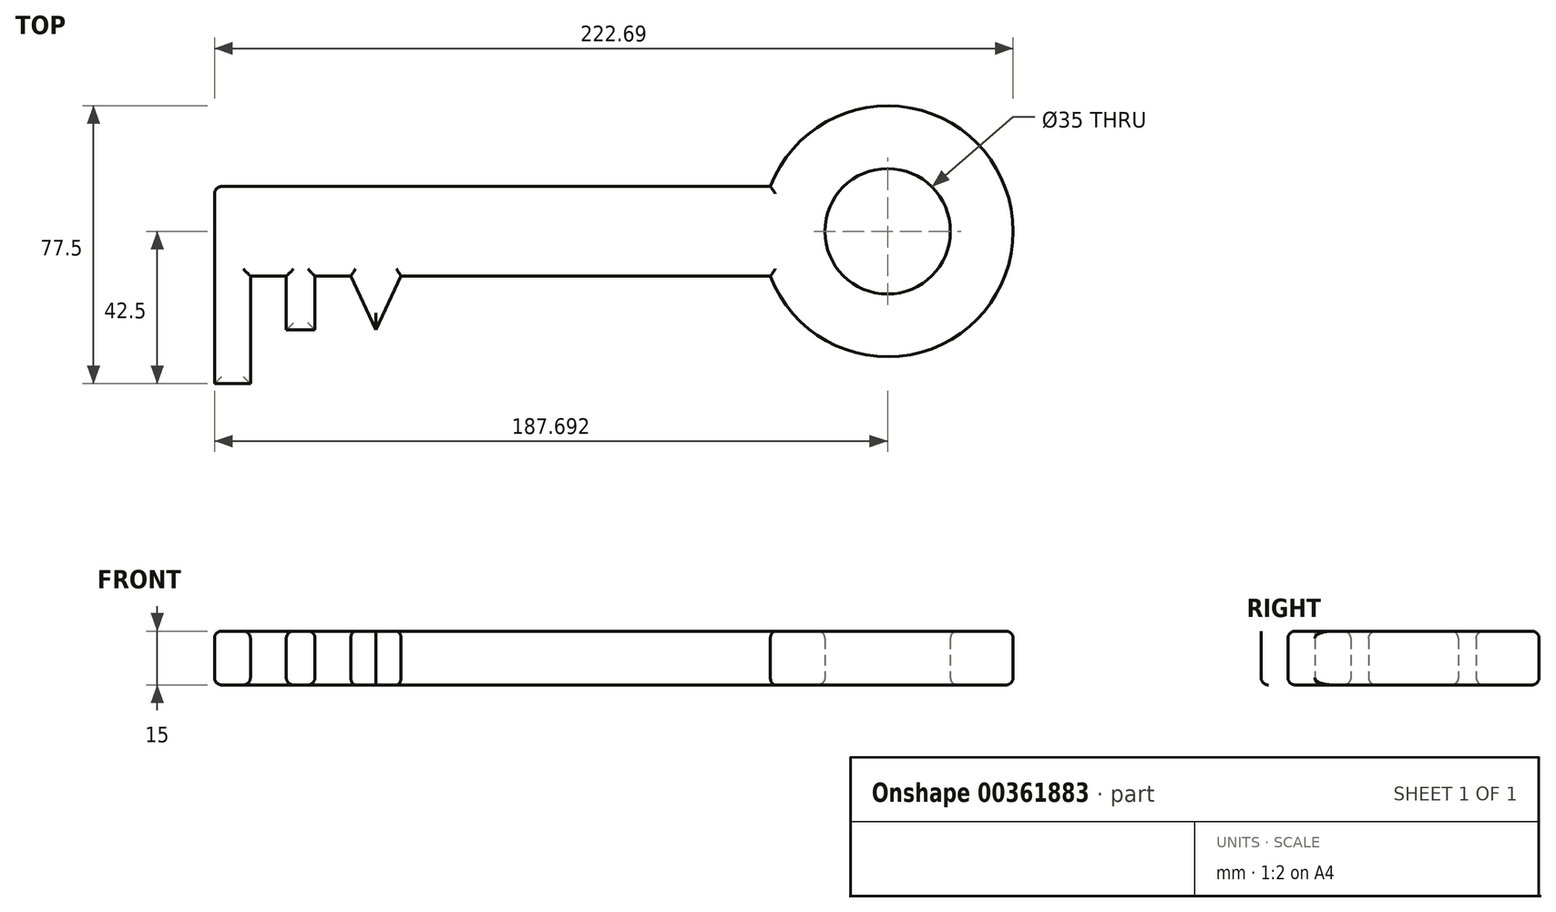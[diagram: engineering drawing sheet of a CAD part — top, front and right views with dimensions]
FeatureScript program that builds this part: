
annotation { "Feature Type Name" : "Feature", "Feature Type Description" : "" }
export const myFeature = defineFeature(function(context is Context, id is Id, definition is map)
    precondition{}
    {
        {
            var Q0;
            Q0=qCreatedBy(makeId("Top.planeOp"),FACE);
            var sketch = newSketch(context, id + "F0", { "sketchPlane" : qUnion([Q0])});
            skLineSegment(sketch, "E0.bottom", {"start": v(0, 25) * mm, "end": v(-155, 25) * mm});
            skLineSegment(sketch, "E0.top", {"start": v(0, 0) * mm, "end": v(-155, 0) * mm});
            skLineSegment(sketch, "E0.left", {"start": v(0, 25) * mm, "end": v(0, 0) * mm});
            skLineSegment(sketch, "E0.right", {"start": v(-155, 25) * mm, "end": v(-155, 0) * mm});
            skLineSegment(sketch, "E1.bottom", {"start": v(-155, 0) * mm, "end": v(-145, 0) * mm});
            skLineSegment(sketch, "E1.top", {"start": v(-155, -30) * mm, "end": v(-145, -30) * mm});
            skLineSegment(sketch, "E1.left", {"start": v(-155, 0) * mm, "end": v(-155, -30) * mm});
            skLineSegment(sketch, "E1.right", {"start": v(-145, 0) * mm, "end": v(-145, -30) * mm});
            skLineSegment(sketch, "E2.bottom", {"start": v(-135, 0) * mm, "end": v(-127, 0) * mm});
            skLineSegment(sketch, "E2.top", {"start": v(-135, -15) * mm, "end": v(-127, -15) * mm});
            skLineSegment(sketch, "E2.left", {"start": v(-135, 0) * mm, "end": v(-135, -15) * mm});
            skLineSegment(sketch, "E2.right", {"start": v(-127, 0) * mm, "end": v(-127, -15) * mm});
            skLineSegment(sketch, "E3", {"start": v(-117, 0) * mm, "end": v(-110, -15) * mm});
            skLineSegment(sketch, "E4", {"start": v(-110, -15) * mm, "end": v(-103, 0) * mm});
            skArc(sketch, "E5", {"start": v(0, 0) * mm, "mid": v(67.7, 12.5) * mm, "end": v(0, 25) * mm});
            skCircle(sketch, "E6", {"center": v(32.7, 12.5) * mm, "radius": 17.5 * mm});
            skLineSegment(sketch, "E7", {"start": v(-155, 12.5) * mm, "end": v(32.7, 12.5) * mm, "construction": true});
            skSolve(sketch);
        }
        {
            var Q0;
            Q0=makeQuery(id+"F0.imprint","IMPRINT",FACE,{"disambiguationData":[TD([[makeQuery(id+"F0.imprint","IMPRINT",EDGE,{"derivedFrom":sQuery(id+"F0.wireOp",EDGE,"E0.bottom")}),1.0]])]});
            var Q1;
            Q1=makeQuery(id+"F0.imprint","IMPRINT",FACE,{"disambiguationData":[TD([[makeQuery(id+"F0.imprint","IMPRINT",EDGE,{"derivedFrom":sQuery(id+"F0.wireOp",EDGE,"E0.left")}),1.0]])]});
            var Q2;
            Q2=makeQuery(id+"F0.imprint","IMPRINT",FACE,{"disambiguationData":[TD([[makeQuery(id+"F0.imprint","IMPRINT",EDGE,{"derivedFrom":sQuery(id+"F0.wireOp",EDGE,"E1.bottom")}),-1.0]])]});
            var Q3;
            Q3=makeQuery(id+"F0.imprint","IMPRINT",FACE,{"disambiguationData":[TD([[makeQuery(id+"F0.imprint","IMPRINT",EDGE,{"derivedFrom":sQuery(id+"F0.wireOp",EDGE,"E2.bottom")}),-1.0]])]});
            var Q4;
            {var subQ0=sQuery(id+"F0.wireOp",EDGE,"E3");Q4=makeQuery(id+"F0.imprint","IMPRINT",FACE,{"disambiguationData":[TD([[makeQuery(id+"F0.imprint","IMPRINT",EDGE,{"derivedFrom":subQ0}),1.0]])]});}
            extrude(context, id + "F1", {"entities" : qUnion([Q0, Q1, Q2, Q3, Q4]), "depth" : 15 * mm});
        }
        {
            var Q0;
            Q0=makeQuery(id+"F1.opExtrude","CAP_EDGE",EDGE,{"disambiguationData":[OSD([sQuery(id+"F0.wireOp",EDGE,"E0.bottom")])],"isStart":false});
            var Q1;
            Q1=makeQuery(id+"F1.opExtrude","CAP_EDGE",EDGE,{"disambiguationData":[OSD([sQuery(id+"F0.wireOp",EDGE,"E0.bottom")])],"isStart":true});
            var Q2;
            Q2=makeQuery(id+"F1.opExtrude","CAP_EDGE",EDGE,{"disambiguationData":[OSD([sQuery(id+"F0.wireOp",EDGE,"E0.right"),sQuery(id+"F0.wireOp",EDGE,"E1.left")])],"isStart":true});
            var Q3;
            Q3=makeQuery(id+"F1.opExtrude","CAP_EDGE",EDGE,{"disambiguationData":[OSD([sQuery(id+"F0.wireOp",EDGE,"E0.right"),sQuery(id+"F0.wireOp",EDGE,"E1.left")])],"isStart":false});
            var Q4;
            {var subQ0=sQuery(id+"F0.wireOp",EDGE,"E0.top");Q4=makeQuery(id+"F1.opExtrude","CAP_EDGE",EDGE,{"disambiguationData":[OSD([subQ0]),TDD([makeQuery(id+"F0.imprint","IMPRINT",EDGE,{"disambiguationData":[TD([[makeQuery(id+"F0.imprint","INTERSECT",VERTEX,{"derivedFrom":[subQ0,sQuery(id+"F0.wireOp",EDGE,"E4")]}),1.0]])],"derivedFrom":subQ0})])],"isStart":true});}
            var Q5;
            Q5=makeQuery(id+"F1.opExtrude","CAP_FACE",FACE,{"disambiguationData":[OSD([sQuery(id+"F0.wireOp",EDGE,"E0.bottom"),sQuery(id+"F0.wireOp",EDGE,"E0.top"),sQuery(id+"F0.wireOp",EDGE,"E0.right"),sQuery(id+"F0.wireOp",EDGE,"E1.top"),sQuery(id+"F0.wireOp",EDGE,"E1.left"),sQuery(id+"F0.wireOp",EDGE,"E1.right"),sQuery(id+"F0.wireOp",EDGE,"E2.top"),sQuery(id+"F0.wireOp",EDGE,"E2.left"),sQuery(id+"F0.wireOp",EDGE,"E2.right"),sQuery(id+"F0.wireOp",EDGE,"E3"),sQuery(id+"F0.wireOp",EDGE,"E4"),sQuery(id+"F0.wireOp",EDGE,"E5"),sQuery(id+"F0.wireOp",EDGE,"E6")])],"isStart":false});
            fillet(context, id + "F2", {"entities" : qUnion([Q0, Q1, Q2, Q3, Q4, Q5]), "radius" : 2 * mm, "tangentPropagation" : true, "allowEdgeOverflow" : false});
        }
        {
            var Q0;
            Q0 = qSketchRegion(id + "F0", true);
            extrude(context, id + "F3", {"entities" : qUnion([Q0]), "operationType" : NewBodyOperationType.ADD, "depth" : 15 * mm});
        }
        {
            var Q0;
            Q0=makeQuery(id+"F3.opExtrude","CAP_EDGE",EDGE,{"disambiguationData":[OSD([sQuery(id+"F0.wireOp",EDGE,"E0.bottom")])],"isStart":false});
            var Q1;
            Q1=makeQuery(id+"F3.opExtrude","CAP_EDGE",EDGE,{"disambiguationData":[OSD([sQuery(id+"F0.wireOp",EDGE,"E0.right"),sQuery(id+"F0.wireOp",EDGE,"E1.left")])],"isStart":false});
            var Q2;
            Q2=makeQuery(id+"F3.opExtrude","CAP_EDGE",EDGE,{"disambiguationData":[OSD([sQuery(id+"F0.wireOp",EDGE,"E1.right")])],"isStart":false});
            var Q3;
            Q3=makeQuery(id+"F3.opExtrude","CAP_EDGE",EDGE,{"disambiguationData":[OSD([sQuery(id+"F0.wireOp",EDGE,"E2.left")])],"isStart":false});
            var Q4;
            Q4=makeQuery(id+"F3.opExtrude","CAP_EDGE",EDGE,{"disambiguationData":[OSD([sQuery(id+"F0.wireOp",EDGE,"E2.right")])],"isStart":false});
            var Q5;
            Q5=makeQuery(id+"F3.opExtrude","CAP_EDGE",EDGE,{"disambiguationData":[OSD([sQuery(id+"F0.wireOp",EDGE,"E3")])],"isStart":false});
            var Q6;
            Q6=makeQuery(id+"F3.opExtrude","CAP_EDGE",EDGE,{"disambiguationData":[OSD([sQuery(id+"F0.wireOp",EDGE,"E4")])],"isStart":false});
            var Q7;
            {var subQ0=sQuery(id+"F0.wireOp",EDGE,"E0.top");Q7=makeQuery(id+"F3.opExtrude","CAP_EDGE",EDGE,{"disambiguationData":[OSD([subQ0]),TDD([makeQuery(id+"F0.imprint","IMPRINT",EDGE,{"disambiguationData":[TD([[makeQuery(id+"F0.imprint","INTERSECT",VERTEX,{"derivedFrom":[subQ0,sQuery(id+"F0.wireOp",EDGE,"E4")]}),1.0]])],"derivedFrom":subQ0})])],"isStart":false});}
            var Q8;
            {var subQ0=sQuery(id+"F0.wireOp",EDGE,"E0.top");Q8=makeQuery(id+"F3.opExtrude","CAP_EDGE",EDGE,{"disambiguationData":[OSD([subQ0]),TDD([makeQuery(id+"F0.imprint","IMPRINT",EDGE,{"disambiguationData":[TD([[makeQuery(id+"F0.imprint","INTERSECT",VERTEX,{"derivedFrom":[subQ0,sQuery(id+"F0.wireOp",EDGE,"E3")]}),-1.0]])],"derivedFrom":subQ0})])],"isStart":false});}
            var Q9;
            {var subQ0=sQuery(id+"F0.wireOp",EDGE,"E0.top");Q9=makeQuery(id+"F3.opExtrude","CAP_EDGE",EDGE,{"disambiguationData":[OSD([subQ0]),TDD([makeQuery(id+"F0.imprint","IMPRINT",EDGE,{"disambiguationData":[TD([[makeQuery(id+"F0.imprint","INTERSECT",VERTEX,{"derivedFrom":[subQ0,sQuery(id+"F0.wireOp",EDGE,"E1.bottom"),sQuery(id+"F0.wireOp",EDGE,"E1.right")]}),1.0]])],"derivedFrom":subQ0})])],"isStart":false});}
            var Q10;
            {var subQ0=sQuery(id+"F0.wireOp",EDGE,"E1.left");var subQ1=sQuery(id+"F0.wireOp",EDGE,"E1.top");Q10=makeQuery(id+"F3.boolean.opBoolean","MERGE",EDGE,{"derivedFrom":[makeQuery(id+"F1.opExtrude","SWEPT_EDGE",EDGE,{"disambiguationData":[OSD([subQ1,subQ0])]}),makeQuery(id+"F3.opExtrude","SWEPT_EDGE",EDGE,{"disambiguationData":[OSD([subQ1,subQ0])]})]});}
            var Q11;
            Q11=makeQuery(id+"F3.opExtrude","CAP_EDGE",EDGE,{"disambiguationData":[OSD([sQuery(id+"F0.wireOp",EDGE,"E0.right"),sQuery(id+"F0.wireOp",EDGE,"E1.left")])],"isStart":true});
            var Q12;
            {var subQ0=sQuery(id+"F0.wireOp",EDGE,"E0.right");var subQ1=sQuery(id+"F0.wireOp",EDGE,"E0.bottom");Q12=makeQuery(id+"F3.boolean.opBoolean","MERGE",EDGE,{"derivedFrom":[makeQuery(id+"F1.opExtrude","SWEPT_EDGE",EDGE,{"disambiguationData":[OSD([subQ1,subQ0])]}),makeQuery(id+"F3.opExtrude","SWEPT_EDGE",EDGE,{"disambiguationData":[OSD([subQ1,subQ0])]})]});}
            var Q13;
            Q13=makeQuery(id+"F3.opExtrude","CAP_EDGE",EDGE,{"disambiguationData":[OSD([sQuery(id+"F0.wireOp",EDGE,"E5")])],"isStart":false});
            var Q14;
            Q14=makeQuery(id+"F3.opExtrude","CAP_EDGE",EDGE,{"disambiguationData":[OSD([sQuery(id+"F0.wireOp",EDGE,"E6")])],"isStart":false});
            var Q15;
            Q15=makeQuery(id+"F1.opExtrude","CAP_EDGE",EDGE,{"disambiguationData":[OSD([sQuery(id+"F0.wireOp",EDGE,"E6")])],"isStart":true});
            var Q16;
            Q16=makeQuery(id+"F1.opExtrude","CAP_EDGE",EDGE,{"disambiguationData":[OSD([sQuery(id+"F0.wireOp",EDGE,"E5")])],"isStart":true});
            var Q17;
            Q17=makeQuery(id+"F3.opExtrude","CAP_EDGE",EDGE,{"disambiguationData":[OSD([sQuery(id+"F0.wireOp",EDGE,"E0.bottom")])],"isStart":true});
            var Q18;
            {var subQ0=sQuery(id+"F0.wireOp",EDGE,"E6");var subQ1=sQuery(id+"F0.wireOp",EDGE,"E5");var subQ2=sQuery(id+"F0.wireOp",EDGE,"E4");var subQ3=sQuery(id+"F0.wireOp",EDGE,"E3");var subQ4=sQuery(id+"F0.wireOp",EDGE,"E2.right");var subQ5=sQuery(id+"F0.wireOp",EDGE,"E2.left");var subQ6=sQuery(id+"F0.wireOp",EDGE,"E2.top");var subQ7=sQuery(id+"F0.wireOp",EDGE,"E1.right");var subQ8=sQuery(id+"F0.wireOp",EDGE,"E1.left");var subQ9=sQuery(id+"F0.wireOp",EDGE,"E1.top");var subQ10=sQuery(id+"F0.wireOp",EDGE,"E0.right");var subQ11=sQuery(id+"F0.wireOp",EDGE,"E0.top");var subQ12=sQuery(id+"F0.wireOp",EDGE,"E0.bottom");Q18=makeQuery(id+"F3.boolean.opBoolean","MERGE",FACE,{"derivedFrom":[makeQuery(id+"F1.opExtrude","CAP_FACE",FACE,{"disambiguationData":[OSD([subQ12,subQ11,subQ10,subQ9,subQ8,subQ7,subQ6,subQ5,subQ4,subQ3,subQ2,subQ1,subQ0])],"isStart":true}),makeQuery(id+"F3.opExtrude","CAP_FACE",FACE,{"disambiguationData":[OSD([subQ12,subQ11,subQ10,subQ9,subQ8,subQ7,subQ6,subQ5,subQ4,subQ3,subQ2,subQ1,subQ0])],"isStart":true})]});}
            fillet(context, id + "F4", {"entities" : qUnion([Q0, Q1, Q2, Q3, Q4, Q5, Q6, Q7, Q8, Q9, Q10, Q11, Q12, Q13, Q14, Q15, Q16, Q17, Q18]), "radius" : 2 * mm, "tangentPropagation" : true, "allowEdgeOverflow" : false});
        }
    });
